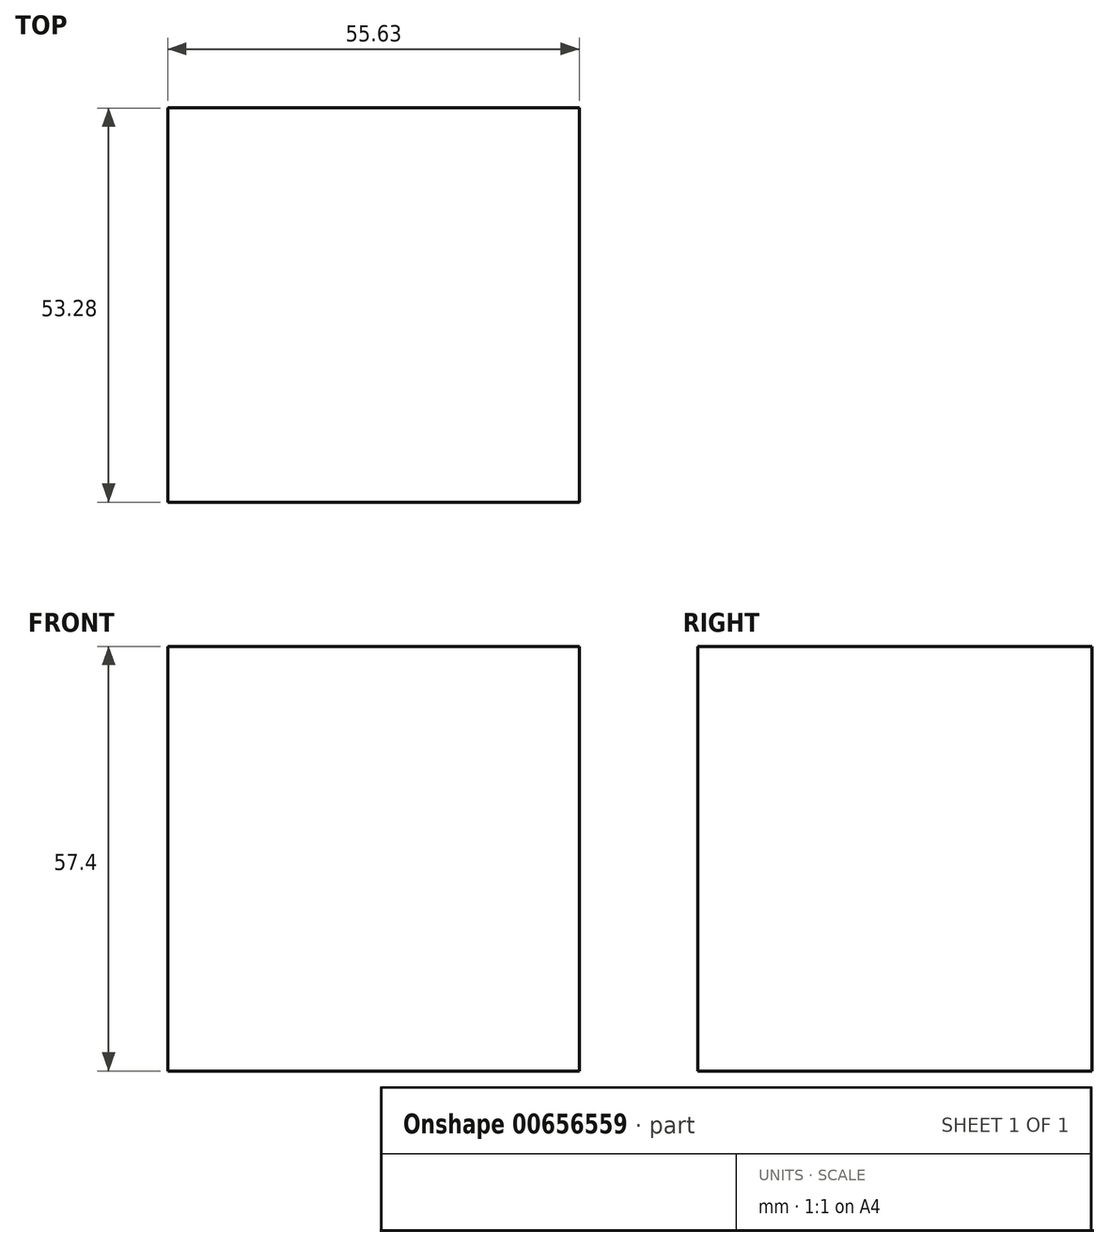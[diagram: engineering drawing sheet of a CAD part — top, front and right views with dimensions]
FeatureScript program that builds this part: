
annotation { "Feature Type Name" : "Feature", "Feature Type Description" : "" }
export const myFeature = defineFeature(function(context is Context, id is Id, definition is map)
    precondition{}
    {
        {
            var Q0;
            Q0=qCreatedBy(makeId("Right.planeOp"),FACE);
            var sketch = newSketch(context, id + "F0", { "sketchPlane" : qUnion([Q0])});
            skLineSegment(sketch, "E0.bottom", {"start": v(-104.7, 114.31) * mm, "end": v(-51.4, 114.31) * mm});
            skLineSegment(sketch, "E0.top", {"start": v(-104.7, 56.9) * mm, "end": v(-51.4, 56.9) * mm});
            skLineSegment(sketch, "E0.left", {"start": v(-104.7, 114.31) * mm, "end": v(-104.7, 56.9) * mm});
            skLineSegment(sketch, "E0.right", {"start": v(-51.4, 114.31) * mm, "end": v(-51.4, 56.9) * mm});
            skSolve(sketch);
        }
        {
            var Q0;
            Q0 = qSketchRegion(id + "F0", true);
            extrude(context, id + "F1", {"entities" : qUnion([Q0]), "depth" : 55.63 * mm, "offsetDistance" : 25.4 * mm});
        }
    });
